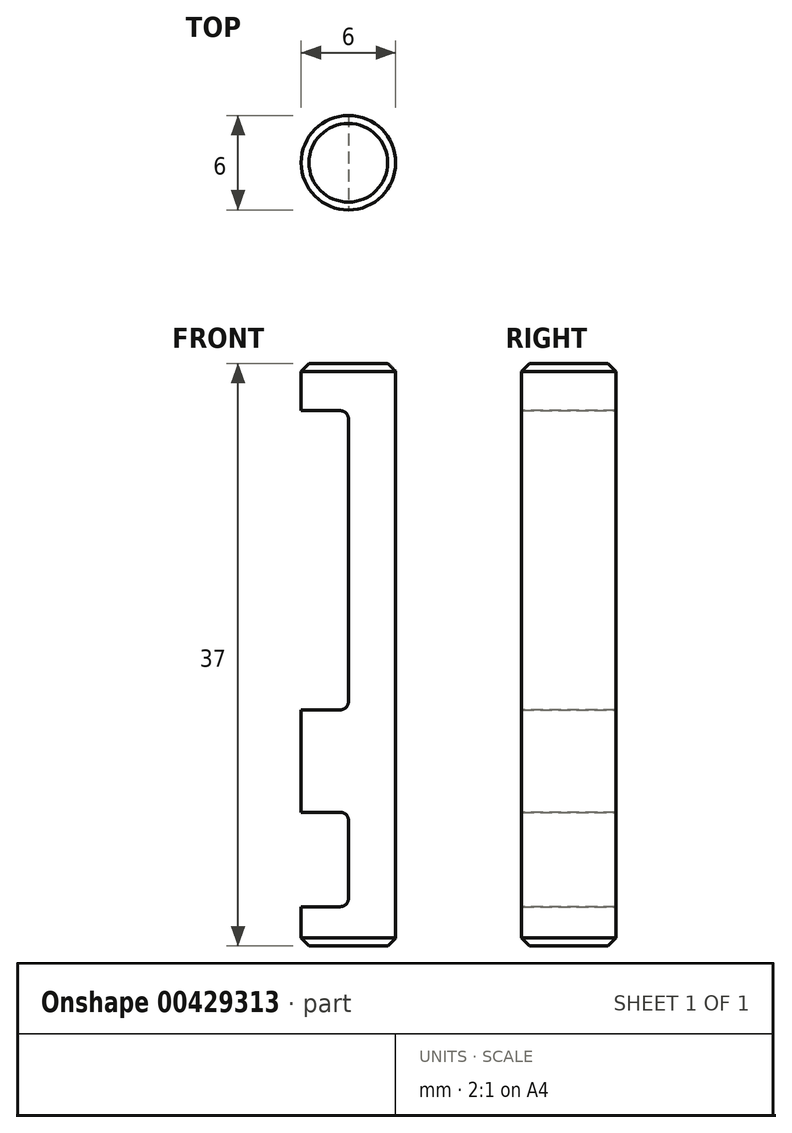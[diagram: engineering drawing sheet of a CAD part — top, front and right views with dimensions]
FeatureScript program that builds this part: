
annotation { "Feature Type Name" : "Feature", "Feature Type Description" : "" }
export const myFeature = defineFeature(function(context is Context, id is Id, definition is map)
    precondition{}
    {
        {
            var Q0;
            Q0=qCreatedBy(makeId("Top.planeOp"),FACE);
            var sketch = newSketch(context, id + "F0", { "sketchPlane" : qUnion([Q0])});
            skCircle(sketch, "E0", {"center": v(0, 0) * mm, "radius": 3 * mm});
            skSolve(sketch);
        }
        {
            var Q0;
            Q0=makeQuery(id+"F0.imprint","IMPRINT",FACE,{"disambiguationData":[TD([[makeQuery(id+"F0.imprint","IMPRINT",EDGE,{"derivedFrom":sQuery(id+"F0.wireOp",EDGE,"E0")}),1.0]])]});
            extrude(context, id + "F1", {"entities" : qUnion([Q0]), "depth" : 37 * mm});
        }
        {
            var Q0;
            Q0=qCreatedBy(makeId("Front.planeOp"),FACE);
            var sketch = newSketch(context, id + "F2", { "sketchPlane" : qUnion([Q0])});
            skLineSegment(sketch, "E1.bottom", {"start": v(-3, 8.5) * mm, "end": v(0, 8.5) * mm});
            skLineSegment(sketch, "E1.top", {"start": v(-3, 2.5) * mm, "end": v(0, 2.5) * mm});
            skLineSegment(sketch, "E1.left", {"start": v(-3, 8.5) * mm, "end": v(-3, 2.5) * mm});
            skLineSegment(sketch, "E1.right", {"start": v(0, 8.5) * mm, "end": v(0, 2.5) * mm});
            skLineSegment(sketch, "E2.bottom", {"start": v(-3, 34) * mm, "end": v(0, 34) * mm});
            skLineSegment(sketch, "E2.top", {"start": v(-3, 15) * mm, "end": v(0, 15) * mm});
            skLineSegment(sketch, "E2.left", {"start": v(-3, 34) * mm, "end": v(-3, 15) * mm});
            skLineSegment(sketch, "E2.right", {"start": v(0, 34) * mm, "end": v(0, 15) * mm});
            skLineSegment(sketch, "E3", {"start": v(-3, 0) * mm, "end": v(-3, 37) * mm, "construction": true});
            skSolve(sketch);
        }
        {
            var Q0;
            Q0=makeQuery(id+"F2.imprint","IMPRINT",FACE,{"disambiguationData":[TD([[makeQuery(id+"F2.imprint","IMPRINT",EDGE,{"derivedFrom":sQuery(id+"F2.wireOp",EDGE,"E2.bottom")}),-1.0]])]});
            var Q1;
            Q1=makeQuery(id+"F2.imprint","IMPRINT",FACE,{"disambiguationData":[TD([[makeQuery(id+"F2.imprint","IMPRINT",EDGE,{"derivedFrom":sQuery(id+"F2.wireOp",EDGE,"E1.bottom")}),-1.0]])]});
            extrude(context, id + "F3", {"entities" : qUnion([Q0, Q1]), "operationType" : NewBodyOperationType.REMOVE, "oppositeDirection" : true, "depth" : 25 * mm, "symmetric" : true});
        }
        {
            var Q0;
            Q0=makeQuery(id+"F1.opExtrude","CAP_FACE",FACE,{"disambiguationData":[OSD([sQuery(id+"F0.wireOp",EDGE,"E0")])],"isStart":false});
            var Q1;
            Q1=makeQuery(id+"F1.opExtrude","CAP_FACE",FACE,{"disambiguationData":[OSD([sQuery(id+"F0.wireOp",EDGE,"E0")])],"isStart":true});
            chamfer(context, id + "F4", {"entities" : qUnion([Q0, Q1]), "width" : 0.5 * mm, "tangentPropagation" : true});
        }
        {
            var Q0;
            Q0=makeQuery(id+"F3.boolean.opBoolean","COPY",EDGE,{"derivedFrom":makeQuery(id+"F3.opExtrude","SWEPT_EDGE",EDGE,{"disambiguationData":[OSD([sQuery(id+"F2.wireOp",EDGE,"E1.bottom"),sQuery(id+"F2.wireOp",EDGE,"E1.right")])]})});
            var Q1;
            Q1=makeQuery(id+"F3.boolean.opBoolean","COPY",EDGE,{"derivedFrom":makeQuery(id+"F3.opExtrude","SWEPT_EDGE",EDGE,{"disambiguationData":[OSD([sQuery(id+"F2.wireOp",EDGE,"E1.top"),sQuery(id+"F2.wireOp",EDGE,"E1.right")])]})});
            var Q2;
            Q2=makeQuery(id+"F3.boolean.opBoolean","COPY",EDGE,{"derivedFrom":makeQuery(id+"F3.opExtrude","SWEPT_EDGE",EDGE,{"disambiguationData":[OSD([sQuery(id+"F2.wireOp",EDGE,"E2.top"),sQuery(id+"F2.wireOp",EDGE,"E2.right")])]})});
            var Q3;
            Q3=makeQuery(id+"F3.boolean.opBoolean","COPY",EDGE,{"derivedFrom":makeQuery(id+"F3.opExtrude","SWEPT_EDGE",EDGE,{"disambiguationData":[OSD([sQuery(id+"F2.wireOp",EDGE,"E2.bottom"),sQuery(id+"F2.wireOp",EDGE,"E2.right")])]})});
            fillet(context, id + "F5", {"entities" : qUnion([Q0, Q1, Q2, Q3]), "radius" : 0.5 * mm, "tangentPropagation" : true, "allowEdgeOverflow" : false});
        }
    });
